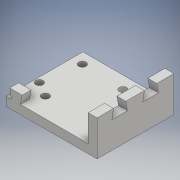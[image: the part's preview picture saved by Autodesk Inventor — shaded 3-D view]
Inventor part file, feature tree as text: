
AUTODESK INVENTOR PART (.ipt)
format: ipt  version: 2017 (Build 210142000, 142)  size: 424,960 bytes
history: native  units: mm
features: extrude x36, sketch x36, shell x1
ambient origin geometry x8: Origin, YZ Plane, XZ Plane, XY Plane, X Axis, Y Axis, Z Axis, Center Point
bodies: Solid1 (feature_tree)
feature tree (73):
  extrude  "Extrusion1"  Depth=20.0mm
  shell  "Shell1"  Thickness=20.0mm
  extrude  "Extrusion2"  Depth=55.0mm
  extrude  "Extrusion3"  TaperAngle=0.0deg  [1 undecoded]
  extrude  "Extrusion4"  Depth=5.0mm
  extrude  "Extrusion5"  TaperAngle=0.0deg  [1 undecoded]
  extrude  "Extrusion6"  Depth=10.0mm TaperAngle=0.0deg
  extrude  "Extrusion7"  Depth=15.0mm TaperAngle=0.0deg
  extrude  "Extrusion9"  Depth=8.5mm
  extrude  "Extrusion10"  Depth=15.0mm TaperAngle=0.0deg
  extrude  "Extrusion11"  Depth=35.46mm
  extrude  "Extrusion12"  Depth=15.0mm TaperAngle=0.0deg
  extrude  "Extrusion13"  Depth=4.5mm
  extrude  "Extrusion14"  Depth=15.0mm TaperAngle=0.0deg
  extrude  "Extrusion15"  Depth=8.5mm
  extrude  "Extrusion16"  Depth=15.0mm TaperAngle=0.0deg
  extrude  "Extrusion17"  Depth=28.505mm
  extrude  "Extrusion18"  Depth=15.0mm TaperAngle=0.0deg
  extrude  "Extrusion19"  Depth=36.0mm
  extrude  "Extrusion20"  Depth=15.0mm TaperAngle=0.0deg
  extrude  "Extrusion23"  Depth=5.0mm
  extrude  "Extrusion21"  Depth=4.1656mm
  extrude  "Extrusion22"  Depth=35.46mm
  extrude  "Extrusion24"  Depth=10.0mm
  extrude  "Extrusion25"  Depth=10.0mm TaperAngle=0.0deg
  extrude  "Extrusion26"  Depth=2.583mm TaperAngle=0.0deg
  extrude  "Extrusion27"  Depth=2.583mm TaperAngle=0.0deg
  extrude  "Extrusion28"  Depth=100.0mm TaperAngle=0.0deg
  extrude  "Extrusion29"  Depth=5.0mm
  extrude  "Extrusion30"  Depth=1.0mm
  extrude  "Extrusion31"  Depth=5.0mm
  extrude  "Extrusion32"  Depth=4.1656mm
  extrude  "Extrusion33"  Depth=6.161mm
  extrude  "Extrusion34"  Depth=4.1656mm
  extrude  "Extrusion35"  Depth=15.906mm
  extrude  "Extrusion36"  Depth=22.5mm TaperAngle=0.0deg
  extrude  "Extrusion37"  Depth=5.0mm TaperAngle=0.0deg
  sketch  "Sketch1"  dims[d0=35.0mm d1=37.0mm d2=20.0mm]
  sketch  "Sketch2"  dims[d3=11.0mm d4=55.0mm]
  sketch  "Sketch3"  dims[d5=26.0mm d6=0.0mm]
  sketch  "Sketch4"  dims[d7=50.0mm d8=0.0mm d9=5.0mm]
  sketch  "Sketch5"  dims[d10=17.0mm d11=0.0mm]
  sketch  "Sketch6"  dims[d12=11.0mm d13=10.0mm d14=0.0mm]
  sketch  "Sketch7"  dims[d15=15.0mm d16=0.0mm d17=15.0mm d18=0.0mm]
  sketch  "Sketch13"  dims[d19=4.1656mm d20=8.5mm]
  sketch  "Sketch14"  dims[d21=11.5mm d22=15.0mm d23=0.0mm]
  sketch  "Sketch15"  dims[d24=4.1656mm d25=35.46mm]
  sketch  "Sketch16"  dims[d26=23.505mm d27=15.0mm d28=0.0mm]
  sketch  "Sketch17"  dims[d29=4.1656mm d30=4.5mm]
  sketch  "Sketch18"  dims[d31=14.0mm d32=15.0mm d33=0.0mm]
  sketch  "Sketch20"  dims[d41=4.1656mm d42=8.5mm]
  sketch  "Sketch21"  dims[d43=11.5mm d44=15.0mm d45=0.0mm]
  sketch  "Sketch22"  dims[d46=4.1656mm d47=28.505mm]
  sketch  "Sketch23"  dims[d48=35.46mm d49=15.0mm d50=0.0mm]
  sketch  "Sketch24"  dims[d51=4.1656mm d52=36.0mm]
  sketch  "Sketch25"  dims[d53=4.5mm d54=15.0mm d55=0.0mm]
  sketch  "Sketch26"  dims[d56=5.0mm d57=50.0mm]
  sketch  "Sketch27"  dims[d58=21.0mm d59=0.0mm d60=4.1656mm]
  sketch  "Sketch28"  dims[d61=23.505mm d62=35.46mm]
  sketch  "Sketch29"  dims[d63=10.0mm d64=0.0mm d65=4.1656mm]
  sketch  "Sketch30"  dims[d67=36.0mm d68=10.0mm d69=0.0mm]
  sketch  "Sketch31"  dims[d70=4.5mm d71=2.583mm d72=0.0mm]
  sketch  "Sketch33"  dims[d73=2.583mm d74=0.0mm d75=2.583mm d76=0.0mm]
  sketch  "Sketch34"  dims[d77=6.917mm d78=100.0mm d79=0.0mm]
  sketch  "Sketch35"  dims[d80=5.0mm d81=5.0mm]
  sketch  "Sketch36"  dims[d83=1.0mm d84=1.0mm]
  sketch  "Sketch38"  dims[d88=22.5mm d89=0.0mm d90=4.1656mm]
  sketch  "Sketch41"  dims[d93=25.0mm d94=0.0mm d95=4.1656mm]
  sketch  "Sketch43"  dims[d96=2.702mm d97=15.906mm]
  sketch  "Sketch44"  dims[d98=25.0mm d99=0.0mm d100=22.5mm d101=0.0mm]
  sketch  "Sketch45"  dims[d102=2.5mm d103=22.5mm d104=0.0mm d105=9.0mm d106=4.0mm d107=5.0mm d108=0.0mm d109=30.0mm d110=0.0mm d111=4.1656mm d112=6.083mm d113=4.0mm d114=30.0mm d115=0.0mm d116=30.0mm d117=0.0mm d118=30.0mm d119=0.0mm d120=30.0mm d121=0.0mm d122=10.0mm d123=0.0mm d124=8.6943mm d125=13.962634mm d126=29.670597mm d127=5.0mm d130=0.0mm d131=34.389mm d132=10.0mm d133=0.0mm d134=10.0mm d135=0.0mm d136=8.6943mm d137=13.962634mm d138=29.670597mm d139=5.0mm d142=0.0mm d143=8.305mm d144=10.0mm d145=0.0mm d153=8.694mm d154=8.694mm d155=10.0mm d156=0.0mm d157=0.0mm d158=50.0mm d159=0.0mm d160=4.1656mm d161=11.0mm d162=11.0mm d163=50.0mm d164=0.0mm d165=3.0mm d166=5.0mm d167=1.0mm d168=7.0mm d169=5.0mm d170=5.0mm d171=0.0mm]
  sketch  "Sketch37"  dims[d85=100.0mm d86=0.0mm d87=5.0mm]
  sketch  "Sketch39"  dims[d91=5.851mm d92=6.161mm]
note: 2 required parameter values undecoded (feature->parameter linkage not recoverable at this tier; creation-order binding heuristic only, values carry confidence <= 0.55)
